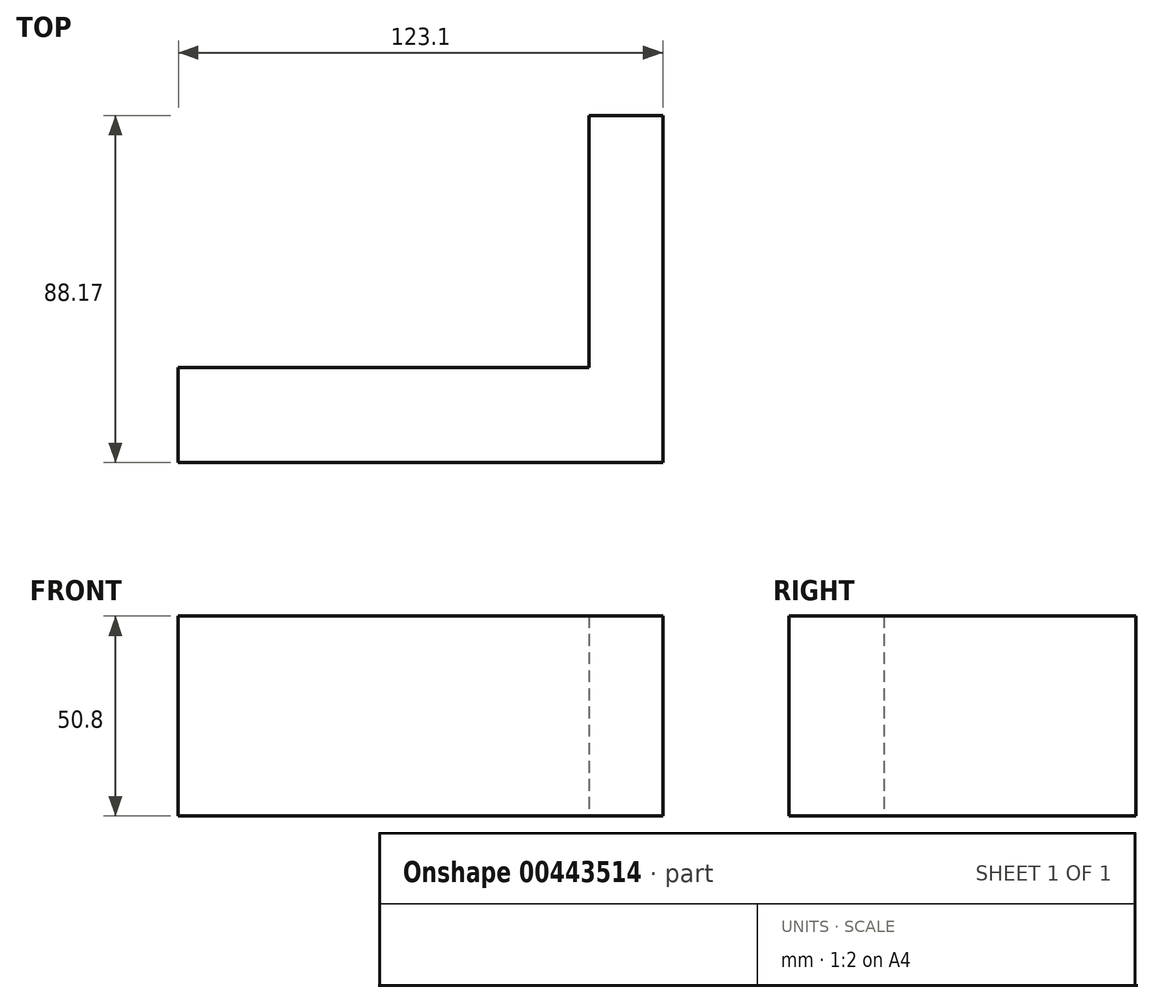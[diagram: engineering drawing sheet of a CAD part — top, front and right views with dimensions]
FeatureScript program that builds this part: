
annotation { "Feature Type Name" : "Feature", "Feature Type Description" : "" }
export const myFeature = defineFeature(function(context is Context, id is Id, definition is map)
    precondition{}
    {
        {
            var Q0;
            Q0=qCreatedBy(makeId("Top.planeOp"),FACE);
            var sketch = newSketch(context, id + "F0", { "sketchPlane" : qUnion([Q0])});
            skLineSegment(sketch, "E0.bottom", {"start": v(-61.55, 12.06) * mm, "end": v(42.84, 12.06) * mm});
            skLineSegment(sketch, "E0.top", {"start": v(-61.55, -12.06) * mm, "end": v(61.55, -12.06) * mm});
            skLineSegment(sketch, "E0.left", {"start": v(-61.55, 12.06) * mm, "end": v(-61.55, -12.06) * mm});
            skLineSegment(sketch, "E0.right", {"start": v(61.55, 12.06) * mm, "end": v(61.55, -12.06) * mm});
            skPoint(sketch, "E0.middle", {"position": v(0, 0) * mm});
            skLineSegment(sketch, "E1.top", {"start": v(61.55, 76.1) * mm, "end": v(42.84, 76.1) * mm});
            skLineSegment(sketch, "E1.left", {"start": v(61.55, 12.06) * mm, "end": v(61.55, 76.1) * mm});
            skLineSegment(sketch, "E1.right", {"start": v(42.84, 12.06) * mm, "end": v(42.84, 76.1) * mm});
            skSolve(sketch);
        }
        {
            var Q0;
            Q0 = qSketchRegion(id + "F0", true);
            extrude(context, id + "F1", {"entities" : qUnion([Q0]), "depth" : 50.8 * mm});
        }
    });
